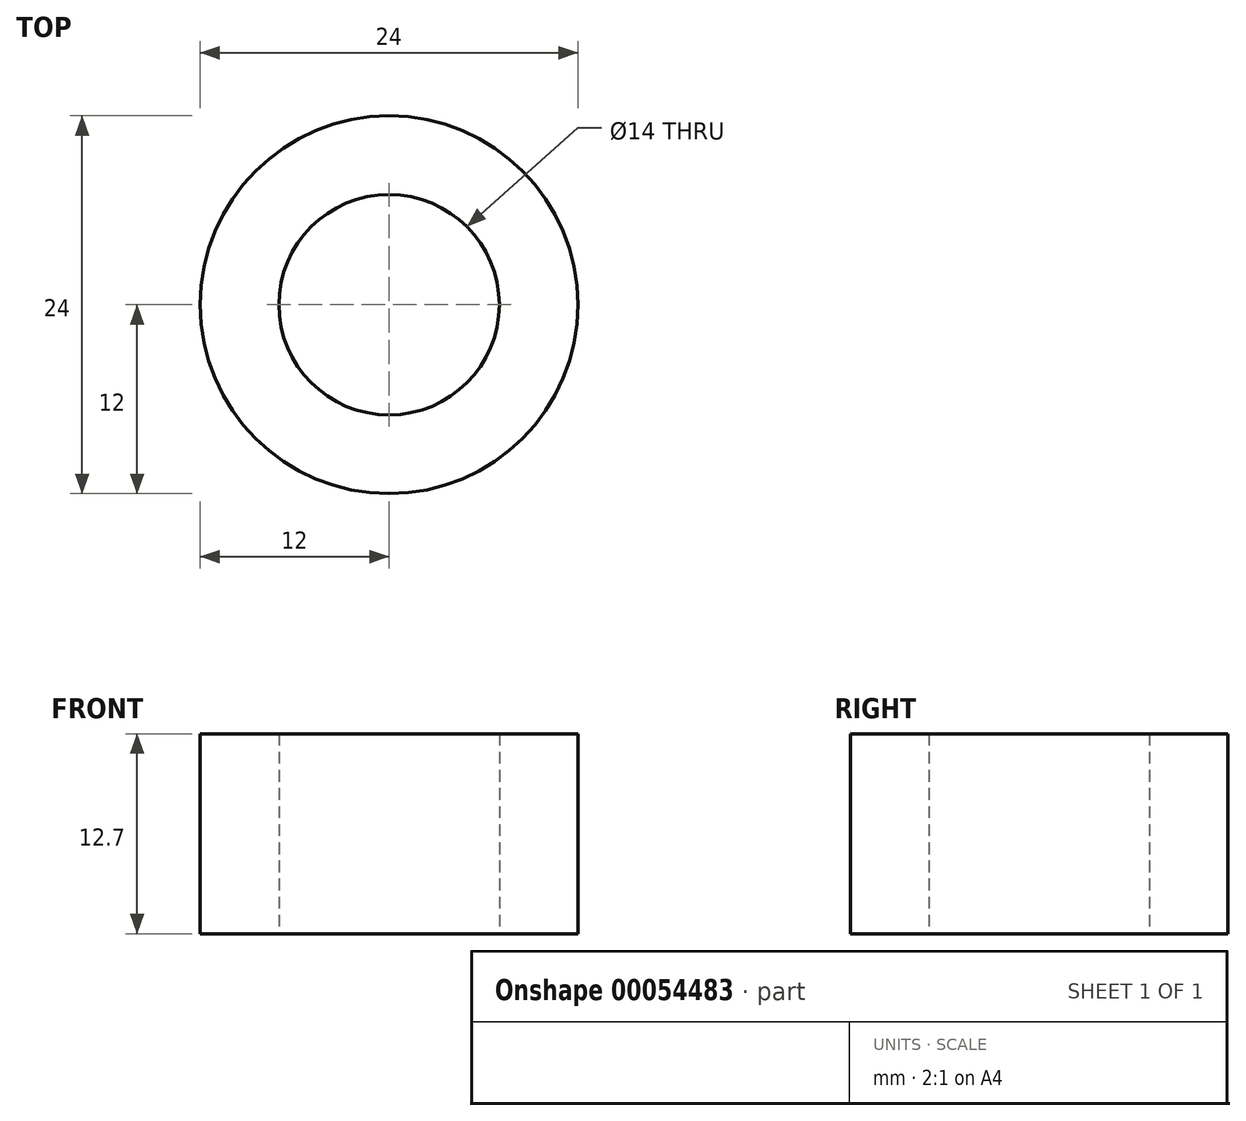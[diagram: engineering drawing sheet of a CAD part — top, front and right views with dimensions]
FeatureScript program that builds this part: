
annotation { "Feature Type Name" : "Feature", "Feature Type Description" : "" }
export const myFeature = defineFeature(function(context is Context, id is Id, definition is map)
    precondition{}
    {
        {
            var Q0;
            Q0=qCreatedBy(makeId("Top.planeOp"),FACE);
            var sketch = newSketch(context, id + "F0", { "sketchPlane" : qUnion([Q0])});
            skCircle(sketch, "E0", {"center": v(0, 0) * mm, "radius": 7 * mm});
            skCircle(sketch, "E1.0", {"center": v(0, 0) * mm, "radius": 12 * mm});
            skSolve(sketch);
        }
        {
            var Q0;
            Q0 = qSketchRegion(id + "F0", true);
            extrude(context, id + "F1", {"entities" : qUnion([Q0]), "depth" : 12.7 * mm});
        }
    });
